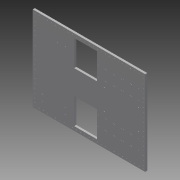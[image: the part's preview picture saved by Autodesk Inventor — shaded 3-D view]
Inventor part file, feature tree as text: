
AUTODESK INVENTOR PART (.ipt)
format: ipt  version: 2014 SP1 (Build 180222100, 222)  size: 257,024 bytes
history: native  units: in
note: dims shown in document units (in); Inventor stores cm internally (conversion verified against a paired STEP export)
features: extrude x1, sketch x1
ambient origin geometry x8: Origin, YZ Plane, XZ Plane, XY Plane, X Axis, Y Axis, Z Axis, Center Point
bodies: Solid1 (feature_tree)
feature tree (2):
  extrude  "Extrusion1"  [1 undecoded]
  sketch  "Sketch1"  dims[d0=0.5in d1=0.0in]
note: 1 required parameter value undecoded (feature->parameter linkage not recoverable at this tier; creation-order binding heuristic only, values carry confidence <= 0.55)
